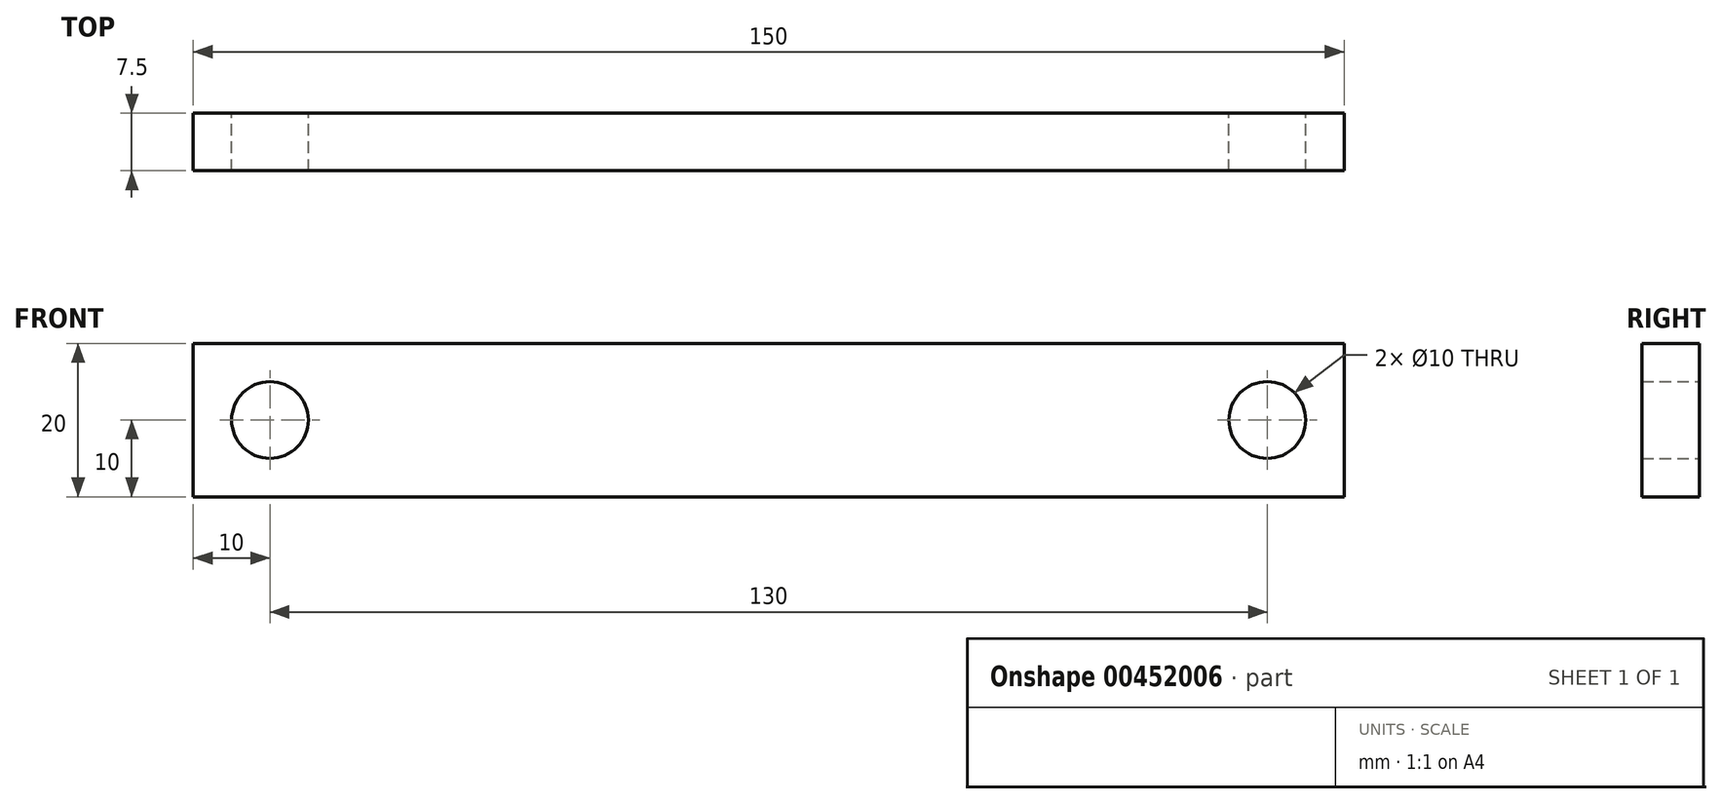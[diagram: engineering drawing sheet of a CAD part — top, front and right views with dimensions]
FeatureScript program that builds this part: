
annotation { "Feature Type Name" : "Feature", "Feature Type Description" : "" }
export const myFeature = defineFeature(function(context is Context, id is Id, definition is map)
    precondition{}
    {
        {
            var Q0;
            Q0=qCreatedBy(makeId("Front.planeOp"),FACE);
            var sketch = newSketch(context, id + "F0", { "sketchPlane" : qUnion([Q0])});
            skLineSegment(sketch, "E0.bottom", {"start": v(-75, 10) * mm, "end": v(75, 10) * mm});
            skLineSegment(sketch, "E0.top", {"start": v(-75, -10) * mm, "end": v(75, -10) * mm});
            skLineSegment(sketch, "E0.left", {"start": v(-75, 10) * mm, "end": v(-75, -10) * mm});
            skLineSegment(sketch, "E0.right", {"start": v(75, 10) * mm, "end": v(75, -10) * mm});
            skCircle(sketch, "E1", {"center": v(-65, 0) * mm, "radius": 5 * mm});
            skCircle(sketch, "E2", {"center": v(65, 0) * mm, "radius": 5 * mm});
            skSolve(sketch);
        }
        {
            var Q0;
            Q0=makeQuery(id+"F0.imprint","IMPRINT",FACE,{"disambiguationData":[TD([[makeQuery(id+"F0.imprint","IMPRINT",EDGE,{"derivedFrom":sQuery(id+"F0.wireOp",EDGE,"E0.bottom")}),-1.0]])]});
            extrude(context, id + "F1", {"entities" : qUnion([Q0]), "endBound" : BoundingType.SYMMETRIC, "depth" : 7.5 * mm});
        }
    });
